# Revit family: Spec Equip_Grabrail_Argent_Advantage_140 deg_ LH
name_source: partatom
category: Specialty Equipment
revit_build: Autodesk Revit 2016 (Build: 20190508_0715(x64)
units: mm (PartAtom-declared; Revit-internal decimal feet)

## family parameters
Always vertical = Yes
Cut with Voids When Loaded = No
OmniClass Number = 23.40.20.21.47
OmniClass Title = Bath Grab Bars
Part Type = Normal
Room Calculation Point = No
Round Connector Dimension = Use Diameter
Shared = No
Work Plane-Based = No

## types (1)
- Polished Stainless Steel (427087LH)
    Body Material = z_Argent_Stainless Steel
    Cost = 0 $
    Description = Advantage 140 deg Left Hand Grab Rail
    IfcExportAs = IfcRailing
    IfcExportType = HANDRAIL
    Manufacturer = Argent
    Manufacturer_Overall Depth = 88.3 mm
    Manufacturer_Overall Height = 602.64 mm
    Manufacturer_Overall Width = 1482.23 mm
    Manufacturer_Spec Code = 427087LH
    Manufacturer_URL__Product Specific = https://www.argentaust.com.au
    Model = 427087LH
    ModifiedIssue_ANZRS = 20200419 $
    Type Comments = Stainless Steel Finish
    URL = https://www.argentaust.com.au
    Uniclass2015Code = Pr_40_20_76_84
    Uniclass2015Title = Support rails
    Uniclass2015Version = Products v1.17

## geometry (parser evidence)
native form markers: Sweep x2
no freeform markers — native parametric forms only
